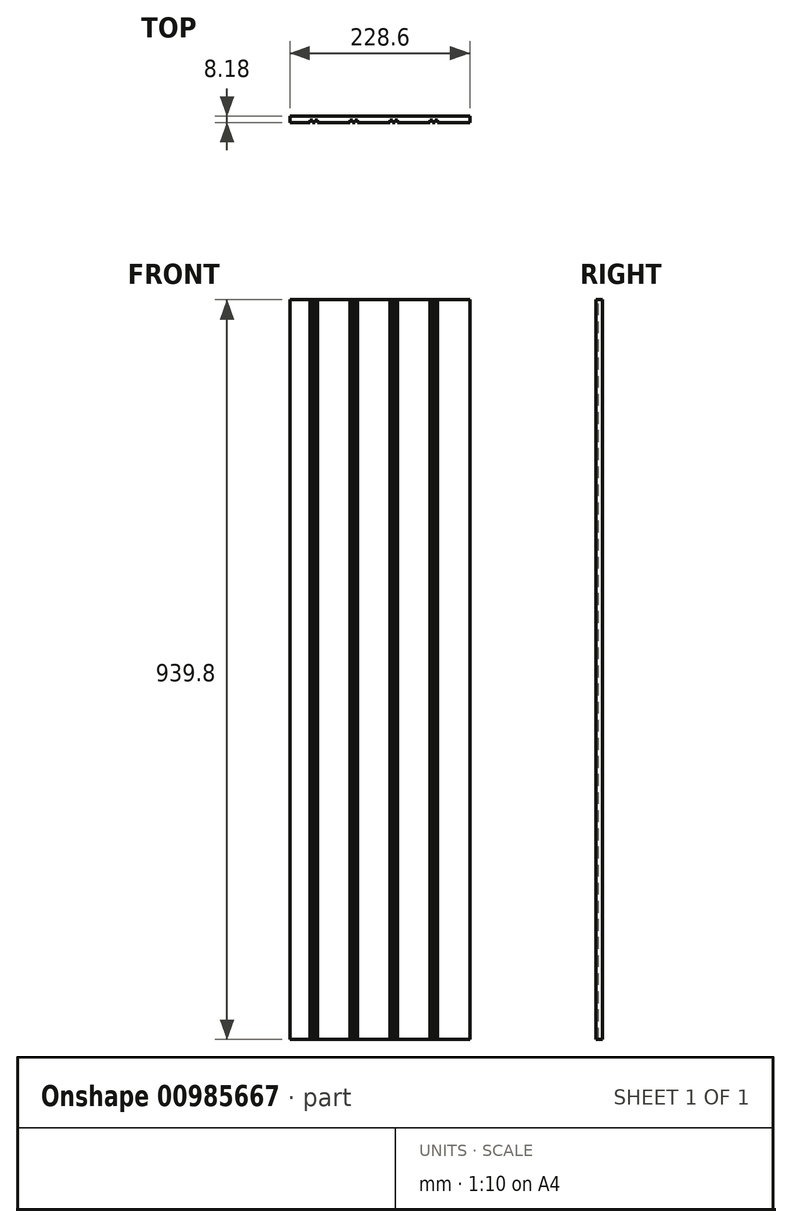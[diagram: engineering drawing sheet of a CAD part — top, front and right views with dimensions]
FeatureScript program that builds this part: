
annotation { "Feature Type Name" : "Feature", "Feature Type Description" : "" }
export const myFeature = defineFeature(function(context is Context, id is Id, definition is map)
    precondition{}
    {
        {
            var Q0;
            Q0=qCreatedBy(makeId("Front.planeOp"),FACE);
            var sketch = newSketch(context, id + "F0", { "sketchPlane" : qUnion([Q0])});
            skLineSegment(sketch, "E0.bottom", {"start": v(114.3, 469.9) * mm, "end": v(-114.3, 469.9) * mm});
            skLineSegment(sketch, "E0.top", {"start": v(114.3, -469.9) * mm, "end": v(-114.3, -469.9) * mm});
            skLineSegment(sketch, "E0.left", {"start": v(114.3, 469.9) * mm, "end": v(114.3, -469.9) * mm});
            skLineSegment(sketch, "E0.right", {"start": v(-114.3, 469.9) * mm, "end": v(-114.3, -469.9) * mm});
            skPoint(sketch, "E0.middle", {"position": v(0, 0) * mm});
            skSolve(sketch);
        }
        {
            var Q0;
            Q0 = qSketchRegion(id + "F0", true);
            extrude(context, id + "F1", {"entities" : qUnion([Q0]), "depth" : 8.18 * mm, "offsetDistance" : 25.4 * mm});
        }
        {
            var Q0;
            Q0=makeQuery(id+"F1.opExtrude","SWEPT_FACE",FACE,{"disambiguationData":[OSD([sQuery(id+"F0.wireOp",EDGE,"E0.bottom")])]});
            var sketch = newSketch(context, id + "F2", { "sketchPlane" : qUnion([Q0])});
            skLineSegment(sketch, "E1.bottom", {"start": v(-88.9, -8.18) * mm, "end": v(-85.73, -8.18) * mm});
            skLineSegment(sketch, "E1.top", {"start": v(-88.9, -5) * mm, "end": v(-85.73, -5) * mm});
            skLineSegment(sketch, "E1.left", {"start": v(-88.9, -8.18) * mm, "end": v(-88.9, -5) * mm});
            skLineSegment(sketch, "E1.right", {"start": v(-85.73, -8.18) * mm, "end": v(-85.73, -5) * mm});
            skLineSegment(sketch, "E2.bottom", {"start": v(-82.55, -5) * mm, "end": v(-79.38, -5) * mm});
            skLineSegment(sketch, "E2.top", {"start": v(-82.55, -8.18) * mm, "end": v(-79.38, -8.18) * mm});
            skLineSegment(sketch, "E2.left", {"start": v(-82.55, -5) * mm, "end": v(-82.55, -8.18) * mm});
            skLineSegment(sketch, "E2.right", {"start": v(-79.38, -5) * mm, "end": v(-79.38, -8.18) * mm});
            skLineSegment(sketch, "E3.1.0.0", {"start": v(-38.1, -5) * mm, "end": v(-34.93, -5) * mm});
            skLineSegment(sketch, "E3.1.0.1", {"start": v(-34.93, -8.18) * mm, "end": v(-34.93, -5) * mm});
            skLineSegment(sketch, "E3.1.0.2", {"start": v(-38.1, -8.18) * mm, "end": v(-38.1, -5) * mm});
            skLineSegment(sketch, "E3.1.0.3", {"start": v(-31.75, -5) * mm, "end": v(-28.58, -5) * mm});
            skLineSegment(sketch, "E3.1.0.4", {"start": v(-28.58, -5) * mm, "end": v(-28.58, -8.18) * mm});
            skLineSegment(sketch, "E3.1.0.5", {"start": v(-31.75, -5) * mm, "end": v(-31.75, -8.18) * mm});
            skLineSegment(sketch, "E3.1.0.6", {"start": v(-31.75, -8.18) * mm, "end": v(-28.58, -8.18) * mm});
            skLineSegment(sketch, "E3.1.0.7", {"start": v(-38.1, -8.18) * mm, "end": v(-34.93, -8.18) * mm});
            skLineSegment(sketch, "E3.2.0.0", {"start": v(12.7, -5) * mm, "end": v(15.87, -5) * mm});
            skLineSegment(sketch, "E3.2.0.1", {"start": v(15.87, -8.18) * mm, "end": v(15.87, -5) * mm});
            skLineSegment(sketch, "E3.2.0.2", {"start": v(12.7, -8.18) * mm, "end": v(12.7, -5) * mm});
            skLineSegment(sketch, "E3.2.0.3", {"start": v(19.05, -5) * mm, "end": v(22.22, -5) * mm});
            skLineSegment(sketch, "E3.2.0.4", {"start": v(22.22, -5) * mm, "end": v(22.22, -8.18) * mm});
            skLineSegment(sketch, "E3.2.0.5", {"start": v(19.05, -5) * mm, "end": v(19.05, -8.18) * mm});
            skLineSegment(sketch, "E3.2.0.6", {"start": v(19.05, -8.18) * mm, "end": v(22.22, -8.18) * mm});
            skLineSegment(sketch, "E3.2.0.7", {"start": v(12.7, -8.18) * mm, "end": v(15.87, -8.18) * mm});
            skLineSegment(sketch, "E3.direction1", {"start": v(-88.9, -5) * mm, "end": v(-38.1, -5) * mm, "construction": true});
            skLineSegment(sketch, "E4.0.3.0", {"start": v(63.5, -5) * mm, "end": v(66.67, -5) * mm});
            skLineSegment(sketch, "E4.3.3.0", {"start": v(66.67, -8.18) * mm, "end": v(66.67, -5) * mm});
            skLineSegment(sketch, "E4.6.3.0", {"start": v(63.5, -8.18) * mm, "end": v(63.5, -5) * mm});
            skLineSegment(sketch, "E4.9.3.0", {"start": v(69.85, -5) * mm, "end": v(73.02, -5) * mm});
            skLineSegment(sketch, "E4.12.3.0", {"start": v(73.02, -5) * mm, "end": v(73.02, -8.18) * mm});
            skLineSegment(sketch, "E4.15.3.0", {"start": v(69.85, -5) * mm, "end": v(69.85, -8.18) * mm});
            skLineSegment(sketch, "E4.18.3.0", {"start": v(69.85, -8.18) * mm, "end": v(73.02, -8.18) * mm});
            skLineSegment(sketch, "E4.21.3.0", {"start": v(63.5, -8.18) * mm, "end": v(66.67, -8.18) * mm});
            skSolve(sketch);
        }
        {
            var Q0;
            Q0 = qSketchRegion(id + "F2", true);
            extrude(context, id + "F3", {"entities" : qUnion([Q0]), "operationType" : NewBodyOperationType.REMOVE, "endBound" : BoundingType.THROUGH_ALL, "oppositeDirection" : true, "depth" : 25.4 * mm, "offsetDistance" : 25.4 * mm});
        }
    });
